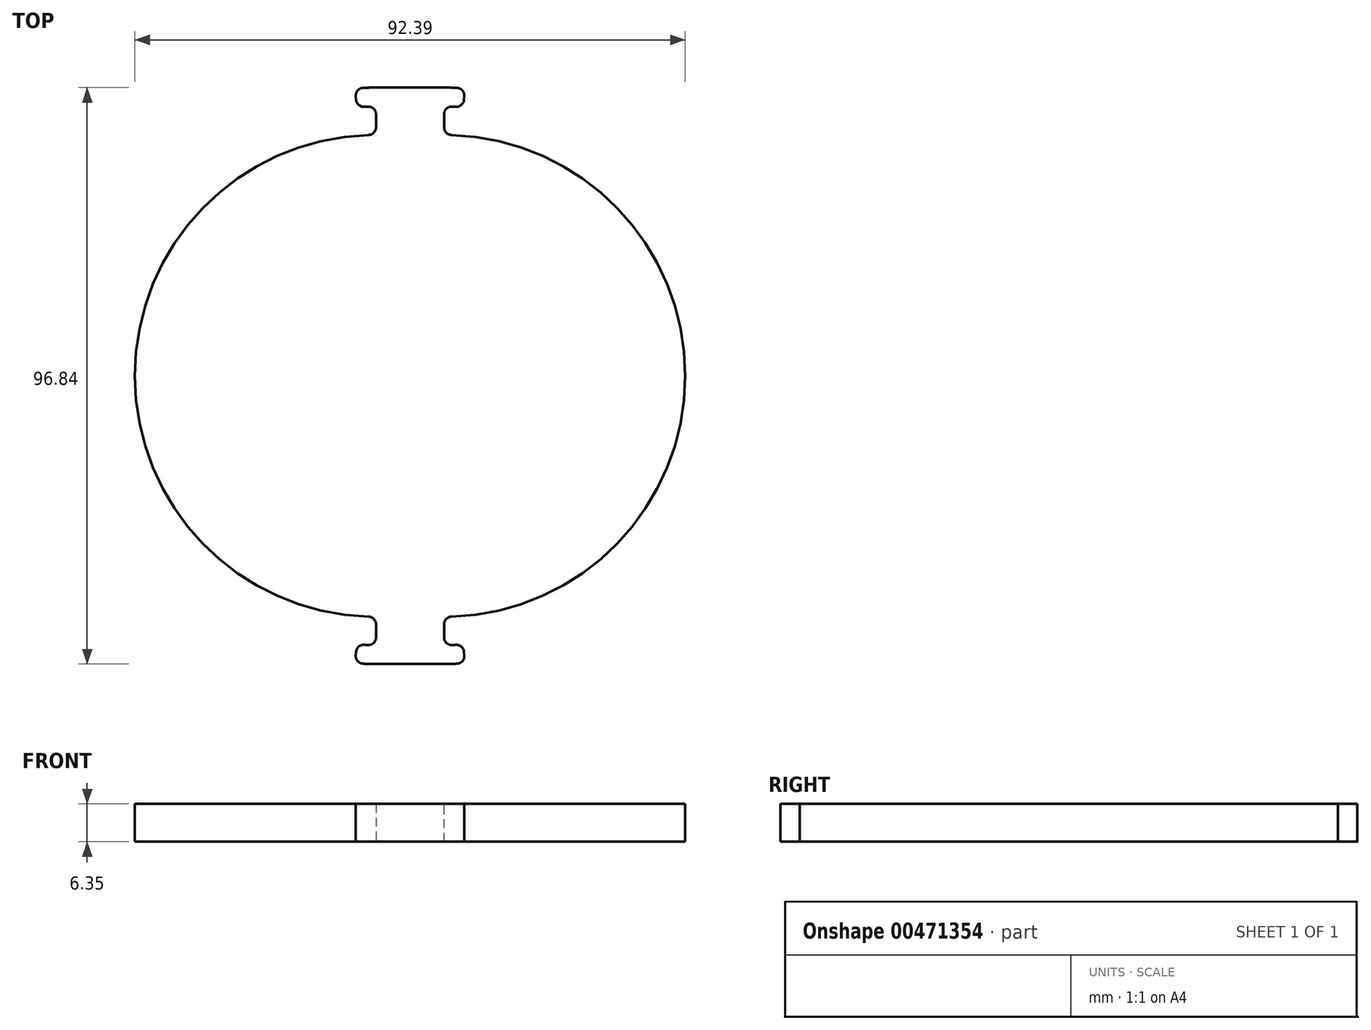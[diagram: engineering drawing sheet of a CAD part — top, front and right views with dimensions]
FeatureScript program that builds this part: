
annotation { "Feature Type Name" : "Feature", "Feature Type Description" : "" }
export const myFeature = defineFeature(function(context is Context, id is Id, definition is map)
    precondition{}
    {
        {
            var Q0;
            Q0=qCreatedBy(makeId("Top.planeOp"),FACE);
            var sketch = newSketch(context, id + "F0", { "sketchPlane" : qUnion([Q0])});
            skArc(sketch, "E0", {"start": v(0, 44.45) * mm, "mid": v(-44.45, 0) * mm, "end": v(0, -44.45) * mm, "construction": true});
            skArc(sketch, "E1", {"start": v(0, 41.28) * mm, "mid": v(-41.28, 0) * mm, "end": v(0, -41.28) * mm, "construction": true});
            skLineSegment(sketch, "E2.bottom", {"start": v(-36.2, 0.8) * mm, "end": v(-36.2, 0.8) * mm});
            skLineSegment(sketch, "E2.top", {"start": v(-36.2, -4.38) * mm, "end": v(-36.2, -4.38) * mm});
            skLineSegment(sketch, "E3.trimOffspring", {"start": v(0, -41.28) * mm, "end": v(0, -41.28) * mm});
            skLineSegment(sketch, "E4.bottom", {"start": v(0, 44.45) * mm, "end": v(11.43, 44.45) * mm, "construction": true});
            skLineSegment(sketch, "E4.top", {"start": v(0, 41.2) * mm, "end": v(11.43, 41.2) * mm, "construction": true});
            skLineSegment(sketch, "E4.left", {"start": v(0, 41.28) * mm, "end": v(0, 41.2) * mm});
            skLineSegment(sketch, "E4.right", {"start": v(11.43, 44.45) * mm, "end": v(11.43, 41.2) * mm, "construction": true});
            skLineSegment(sketch, "E5.bottom", {"start": v(0, -44.45) * mm, "end": v(11.43, -44.45) * mm, "construction": true});
            skLineSegment(sketch, "E5.top", {"start": v(0, -41.28) * mm, "end": v(11.43, -41.28) * mm, "construction": true});
            skLineSegment(sketch, "E5.right", {"start": v(11.43, -44.45) * mm, "end": v(11.43, -41.28) * mm, "construction": true});
            skPoint(sketch, "E6", {"position": v(5.72, 0) * mm});
            skLineSegment(sketch, "E7", {"start": v(5.72, 41.2) * mm, "end": v(5.71, -41.28) * mm, "construction": true});
            skArc(sketch, "E8.MirrorCS", {"start": v(11.43, 41.28) * mm, "mid": v(52.7, 0) * mm, "end": v(11.43, -41.28) * mm, "construction": true});
            skArc(sketch, "E9.0", {"start": v(11.43, 40.48) * mm, "mid": v(51.91, 0) * mm, "end": v(11.43, -40.48) * mm});
            skArc(sketch, "E10.0", {"start": v(0, 40.48) * mm, "mid": v(-40.48, 0) * mm, "end": v(0, -40.48) * mm});
            skLineSegment(sketch, "E11", {"start": v(0, -40.48) * mm, "end": v(0, -45.24) * mm});
            skLineSegment(sketch, "E12", {"start": v(11.43, -40.48) * mm, "end": v(11.43, -45.24) * mm});
            skLineSegment(sketch, "E13", {"start": v(0, -48.42) * mm, "end": v(11.43, -48.42) * mm});
            skArc(sketch, "E14", {"start": v(11.43, -48.42) * mm, "mid": v(13.18, -48.38) * mm, "end": v(14.93, -48.27) * mm});
            skArc(sketch, "E15.0", {"start": v(11.43, -45.24) * mm, "mid": v(13.05, -45.2) * mm, "end": v(14.66, -45.1) * mm});
            skLineSegment(sketch, "E16", {"start": v(11.43, -44.45) * mm, "end": v(14.6, -44.45) * mm, "construction": true});
            skLineSegment(sketch, "E17", {"start": v(14.66, -45.1) * mm, "end": v(14.93, -48.27) * mm});
            skArc(sketch, "E18.MirrorCS", {"start": v(0, -45.24) * mm, "mid": v(-1.62, -45.2) * mm, "end": v(-3.23, -45.1) * mm});
            skLineSegment(sketch, "E19.MirrorCS", {"start": v(-3.23, -45.1) * mm, "end": v(-3.5, -48.27) * mm});
            skArc(sketch, "E20.MirrorCS", {"start": v(0, -48.42) * mm, "mid": v(-1.75, -48.38) * mm, "end": v(-3.5, -48.27) * mm});
            skLineSegment(sketch, "E21.MirrorCS", {"start": v(0, 48.42) * mm, "end": v(11.43, 48.42) * mm});
            skLineSegment(sketch, "E22.MirrorCS", {"start": v(-3.23, 45.1) * mm, "end": v(-3.5, 48.27) * mm});
            skArc(sketch, "E23.MirrorCS", {"start": v(0, 45.24) * mm, "mid": v(-1.62, 45.2) * mm, "end": v(-3.23, 45.1) * mm});
            skArc(sketch, "E24.MirrorCS", {"start": v(0, 48.42) * mm, "mid": v(-1.75, 48.38) * mm, "end": v(-3.5, 48.27) * mm});
            skArc(sketch, "E25.MirrorCS", {"start": v(11.43, 45.24) * mm, "mid": v(13.05, 45.2) * mm, "end": v(14.66, 45.1) * mm});
            skLineSegment(sketch, "E26.MirrorCS", {"start": v(14.66, 45.1) * mm, "end": v(14.93, 48.27) * mm});
            skArc(sketch, "E27.MirrorCS", {"start": v(11.43, 48.42) * mm, "mid": v(13.18, 48.38) * mm, "end": v(14.93, 48.27) * mm});
            skLineSegment(sketch, "E28.MirrorCS", {"start": v(11.43, 40.48) * mm, "end": v(11.43, 45.24) * mm});
            skLineSegment(sketch, "E29.MirrorCS", {"start": v(0, 40.48) * mm, "end": v(0, 45.24) * mm});
            skLineSegment(sketch, "E30", {"start": v(0, 40.48) * mm, "end": v(11.43, 40.48) * mm, "construction": true});
            skSolve(sketch);
        }
        {
            var Q0;
            Q0 = qSketchRegion(id + "F0", true);
            extrude(context, id + "F1", {"entities" : qUnion([Q0]), "depth" : 6.35 * mm, "offsetDistance" : 25.4 * mm});
        }
        {
            var Q0;
            Q0=makeQuery(id+"F1.opExtrude","SWEPT_EDGE",EDGE,{"disambiguationData":[OSD([sQuery(id+"F0.wireOp",EDGE,"E10.0"),sQuery(id+"F0.wireOp",EDGE,"E11")])]});
            var Q1;
            Q1=makeQuery(id+"F1.opExtrude","SWEPT_EDGE",EDGE,{"disambiguationData":[OSD([sQuery(id+"F0.wireOp",EDGE,"E9.0"),sQuery(id+"F0.wireOp",EDGE,"E12")])]});
            var Q2;
            Q2=makeQuery(id+"F1.opExtrude","SWEPT_EDGE",EDGE,{"disambiguationData":[OSD([sQuery(id+"F0.wireOp",EDGE,"E14"),sQuery(id+"F0.wireOp",EDGE,"E17")])]});
            var Q3;
            Q3=makeQuery(id+"F1.opExtrude","SWEPT_EDGE",EDGE,{"disambiguationData":[OSD([sQuery(id+"F0.wireOp",EDGE,"E15.0"),sQuery(id+"F0.wireOp",EDGE,"E17")])]});
            var Q4;
            Q4=makeQuery(id+"F1.opExtrude","SWEPT_EDGE",EDGE,{"disambiguationData":[OSD([sQuery(id+"F0.wireOp",EDGE,"E19.MirrorCS"),sQuery(id+"F0.wireOp",EDGE,"E20.MirrorCS")])]});
            var Q5;
            Q5=makeQuery(id+"F1.opExtrude","SWEPT_EDGE",EDGE,{"disambiguationData":[OSD([sQuery(id+"F0.wireOp",EDGE,"E18.MirrorCS"),sQuery(id+"F0.wireOp",EDGE,"E19.MirrorCS")])]});
            var Q6;
            Q6=makeQuery(id+"F1.opExtrude","SWEPT_EDGE",EDGE,{"disambiguationData":[OSD([sQuery(id+"F0.wireOp",EDGE,"E25.MirrorCS"),sQuery(id+"F0.wireOp",EDGE,"E26.MirrorCS")])]});
            var Q7;
            Q7=makeQuery(id+"F1.opExtrude","SWEPT_EDGE",EDGE,{"disambiguationData":[OSD([sQuery(id+"F0.wireOp",EDGE,"E26.MirrorCS"),sQuery(id+"F0.wireOp",EDGE,"E27.MirrorCS")])]});
            var Q8;
            Q8=makeQuery(id+"F1.opExtrude","SWEPT_EDGE",EDGE,{"disambiguationData":[OSD([sQuery(id+"F0.wireOp",EDGE,"E22.MirrorCS"),sQuery(id+"F0.wireOp",EDGE,"E24.MirrorCS")])]});
            var Q9;
            Q9=makeQuery(id+"F1.opExtrude","SWEPT_EDGE",EDGE,{"disambiguationData":[OSD([sQuery(id+"F0.wireOp",EDGE,"E22.MirrorCS"),sQuery(id+"F0.wireOp",EDGE,"E23.MirrorCS")])]});
            var Q10;
            Q10=makeQuery(id+"F1.opExtrude","SWEPT_EDGE",EDGE,{"disambiguationData":[OSD([sQuery(id+"F0.wireOp",EDGE,"E23.MirrorCS"),sQuery(id+"F0.wireOp",EDGE,"E29.MirrorCS")])]});
            var Q11;
            Q11=makeQuery(id+"F1.opExtrude","SWEPT_EDGE",EDGE,{"disambiguationData":[OSD([sQuery(id+"F0.wireOp",EDGE,"E10.0"),sQuery(id+"F0.wireOp",EDGE,"E29.MirrorCS")])]});
            var Q12;
            Q12=makeQuery(id+"F1.opExtrude","SWEPT_EDGE",EDGE,{"disambiguationData":[OSD([sQuery(id+"F0.wireOp",EDGE,"E12"),sQuery(id+"F0.wireOp",EDGE,"E15.0")])]});
            var Q13;
            Q13=makeQuery(id+"F1.opExtrude","SWEPT_EDGE",EDGE,{"disambiguationData":[OSD([sQuery(id+"F0.wireOp",EDGE,"E11"),sQuery(id+"F0.wireOp",EDGE,"E18.MirrorCS")])]});
            var Q14;
            Q14=makeQuery(id+"F1.opExtrude","SWEPT_EDGE",EDGE,{"disambiguationData":[OSD([sQuery(id+"F0.wireOp",EDGE,"E9.0"),sQuery(id+"F0.wireOp",EDGE,"E28.MirrorCS")])]});
            var Q15;
            Q15=makeQuery(id+"F1.opExtrude","SWEPT_EDGE",EDGE,{"disambiguationData":[OSD([sQuery(id+"F0.wireOp",EDGE,"E25.MirrorCS"),sQuery(id+"F0.wireOp",EDGE,"E28.MirrorCS")])]});
            fillet(context, id + "F2", {"entities" : qUnion([Q0, Q1, Q2, Q3, Q4, Q5, Q6, Q7, Q8, Q9, Q10, Q11, Q12, Q13, Q14, Q15]), "radius" : 1.27 * mm, "tangentPropagation" : true, "allowEdgeOverflow" : false});
        }
    });
